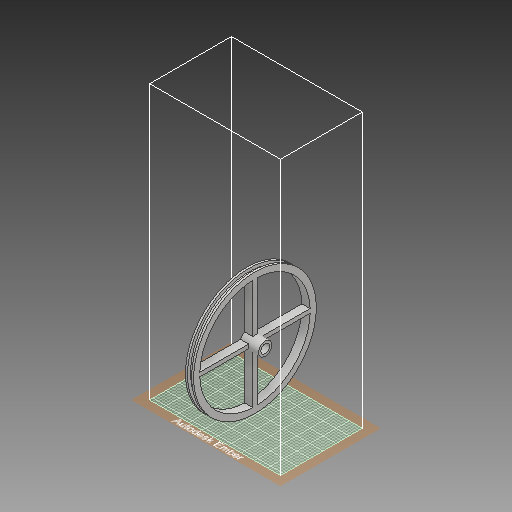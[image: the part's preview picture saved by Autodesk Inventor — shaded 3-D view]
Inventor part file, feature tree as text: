
AUTODESK INVENTOR PART (.ipt)
format: ipt  version: 2018 (Build 220112000, 112)  size: 389,632 bytes
history: native  units: mm
features: extrude x10, sketch x10, fillet x2, pattern_circular x1
ambient origin geometry x8: Origin, YZ Plane, XZ Plane, XY Plane, X Axis, Y Axis, Z Axis, Center Point
bodies: Solid1 (feature_tree)
feature tree (23):
  extrude  "Extrusion1"  Depth=2.0mm TaperAngle=0.0deg
  extrude  "Extrusion2"  Depth=1.0mm TaperAngle=0.0deg
  extrude  "Extrusion3"  Depth=1.0mm TaperAngle=0.0deg
  extrude  "Extrusion4"  Depth=10.0mm TaperAngle=0.0deg
  extrude  "Extrusion5"  Depth=6.5mm
  extrude  "Extrusion6"  Depth=1.0mm
  pattern_circular  "Circular Pattern1"  Count=4 Angle=360.0deg
  extrude  "Extrusion7"  Depth=5.0mm
  extrude  "Extrusion8"  Depth=2.0mm TaperAngle=0.0deg
  extrude  "Extrusion9"  Depth=4.5mm
  extrude  "Extrusion10"  Depth=2.0mm
  fillet  "Fillet1"  Radius=5.0mm
  fillet  "Fillet2"  Radius=4.5mm
  sketch  "Sketch1"  dims[d0=57.0mm d1=2.0mm d2=0.0mm]
  sketch  "Sketch2"  dims[d3=60.0mm d4=1.0mm d5=0.0mm]
  sketch  "Sketch3"  dims[d6=60.0mm d7=1.0mm d8=0.0mm]
  sketch  "Sketch4"  dims[d9=54.0mm d10=10.0mm d11=0.0mm]
  sketch  "Sketch5"  dims[d12=4.25mm d13=6.5mm]
  sketch  "Sketch6"  dims[d14=4.0mm d15=0.0mm d16=1.0mm]
  sketch  "Sketch7"  dims[d17=2.0mm]
  sketch  "Sketch8"  dims[d18=4.0mm d19=0.0mm d20=40.0mm d21=360.0deg]
  sketch  "Sketch9"  dims[d23=5.0mm d24=0.0mm d25=9.0mm]
  sketch  "Sketch10"  dims[d26=4.25mm d27=9.0mm d28=0.0mm d29=4.5mm d30=7.0mm d31=5.0mm d32=0.0mm d33=4.5mm d34=5000.0mm d35=0.0mm d36=2.0mm d37=2.0mm]
